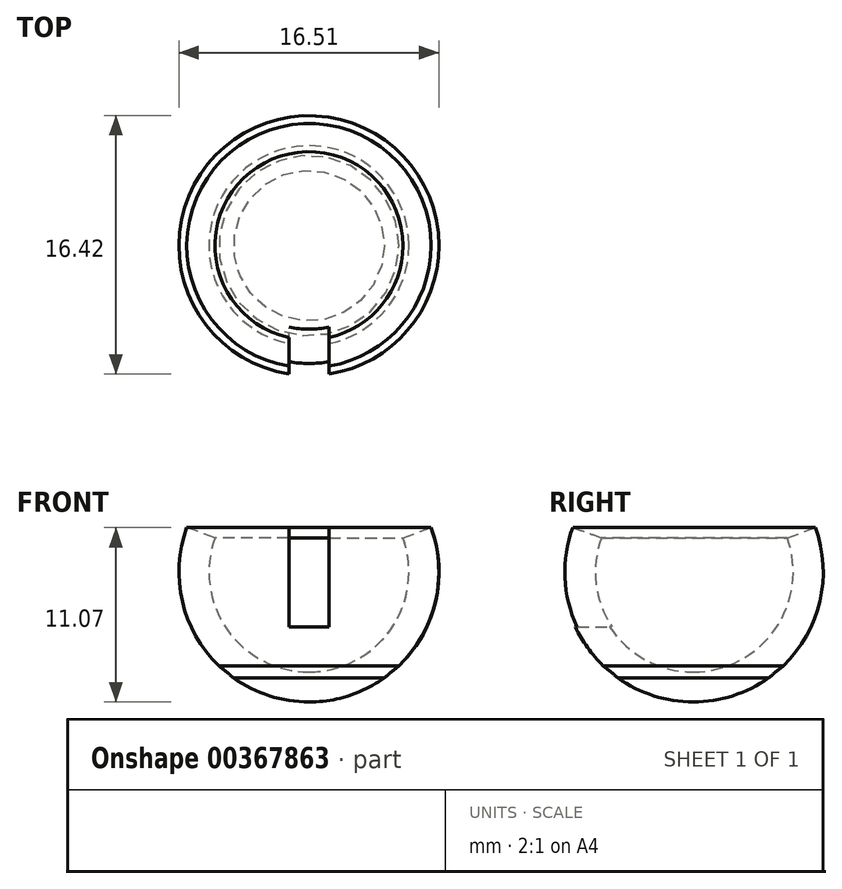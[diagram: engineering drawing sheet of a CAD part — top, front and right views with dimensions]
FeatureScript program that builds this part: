
annotation { "Feature Type Name" : "Feature", "Feature Type Description" : "" }
export const myFeature = defineFeature(function(context is Context, id is Id, definition is map)
    precondition{}
    {
        {
            var Q0;
            Q0=qCreatedBy(makeId("Front.planeOp"),FACE);
            var sketch = newSketch(context, id + "F0", { "sketchPlane" : qUnion([Q0])});
            skLineSegment(sketch, "E0.0", {"start": v(71.22, -1.63) * mm, "end": v(-71.22, -1.63) * mm});
            skLineSegment(sketch, "E1", {"start": v(0, 13.61) * mm, "end": v(0, -1.63) * mm});
            skLineSegment(sketch, "E2.bottom", {"start": v(0, -1.63) * mm, "end": v(0.17, -1.63) * mm});
            skLineSegment(sketch, "E2.top", {"start": v(0, -4.17) * mm, "end": v(1.9, -4.17) * mm});
            skLineSegment(sketch, "E2.left", {"start": v(0, -1.63) * mm, "end": v(0, -4.17) * mm});
            skLineSegment(sketch, "E3", {"start": v(1.9, -4.17) * mm, "end": v(2, -1.63) * mm});
            skArc(sketch, "E4", {"start": v(0, 1.76) * mm, "mid": v(8.26, 10.01) * mm, "end": v(0, 18.27) * mm});
            skLineSegment(sketch, "E5", {"start": v(0, 13.61) * mm, "end": v(0, 18.27) * mm});
            skArc(sketch, "E6.0", {"start": v(0, 3.66) * mm, "mid": v(6.35, 10.01) * mm, "end": v(0, 16.36) * mm});
            skLineSegment(sketch, "E7", {"start": v(0, 10.01) * mm, "end": v(9.82, 13.58) * mm});
            skFitSpline(sketch, "E8", {"points": [v(5.72, 4.06) * mm, v(3.3, 1.68) * mm, v(3.22, 0) * mm, v(6.38, -1.63) * mm], "startDerivative": vector(-8, -6.66) * mm, "endDerivative": vector(12.91, -3.5) * mm});
            skSolve(sketch);
        }
        {
            var Q0;
            Q0=qCreatedBy(makeId("Front.planeOp"),FACE);
            var sketch = newSketch(context, id + "F1", { "sketchPlane" : qUnion([Q0])});
            skLineSegment(sketch, "E9.0", {"start": v(-6.86, 12.88) * mm, "end": v(6.86, 12.88) * mm});
            skLineSegment(sketch, "E10", {"start": v(0, 12.88) * mm, "end": v(0, 17.33) * mm, "construction": true});
            skLineSegment(sketch, "E11.bottom", {"start": v(0, 12.88) * mm, "end": v(1.27, 12.88) * mm});
            skLineSegment(sketch, "E11.top", {"start": v(0, 6.53) * mm, "end": v(1.27, 6.53) * mm});
            skLineSegment(sketch, "E11.left", {"start": v(0, 12.88) * mm, "end": v(0, 6.53) * mm});
            skLineSegment(sketch, "E11.right", {"start": v(1.27, 12.88) * mm, "end": v(1.27, 6.53) * mm});
            skLineSegment(sketch, "E12.MirrorCS", {"start": v(-1.27, 12.88) * mm, "end": v(-1.27, 6.53) * mm});
            skLineSegment(sketch, "E13.MirrorCS", {"start": v(0, 6.53) * mm, "end": v(-1.27, 6.53) * mm});
            skSolve(sketch);
        }
        {
            var Q0;
            {var subQ1=sQuery(id+"F0.wireOp",EDGE,"E1");var subQ6=sQuery(id+"F0.wireOp",EDGE,"E4");var subQ9=makeQuery(id+"F0.imprint","INTERSECT",VERTEX,{"derivedFrom":[subQ1,subQ6]});Q0=makeQuery(id+"F0.imprint","IMPRINT",FACE,{"disambiguationData":[TD([[makeQuery(id+"F0.imprint","IMPRINT",EDGE,{"disambiguationData":[TD([[subQ9,1.0]])],"derivedFrom":subQ1}),1.0]])]});}
            var Q1;
            {var subQ0=sQuery(id+"F0.wireOp",EDGE,"E2.bottom");Q1=makeQuery(id+"F0.imprint","IMPRINT",FACE,{"disambiguationData":[TD([[makeQuery(id+"F0.imprint","IMPRINT",EDGE,{"derivedFrom":subQ0}),1.0]])]});}
            var Q2;
            {var subQ0=sQuery(id+"F0.wireOp",EDGE,"E2.bottom");Q2=makeQuery(id+"F0.imprint","IMPRINT",FACE,{"disambiguationData":[TD([[makeQuery(id+"F0.imprint","IMPRINT",EDGE,{"derivedFrom":subQ0}),-1.0]])]});}
            var Q3;
            Q3=sQuery(id+"F0.wireOp",EDGE,"E1");
            revolve(context, id + "F2", {"entities" : qUnion([Q0, Q1, Q2]), "axis" : qUnion([Q3]), "revolveType" : RevolveType.FULL});
        }
        {
            var Q0;
            Q0 = qSketchRegion(id + "F1", true);
            extrude(context, id + "F3", {"entities" : qUnion([Q0]), "operationType" : NewBodyOperationType.REMOVE, "depth" : 25.4 * mm});
        }
    });
